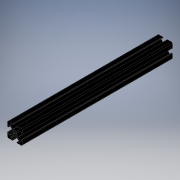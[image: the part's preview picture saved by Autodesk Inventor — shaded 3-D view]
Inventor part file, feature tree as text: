
AUTODESK INVENTOR PART (.ipt)
format: ipt  version: 2019 (Build 230136000, 136)  size: 237,056 bytes
history: native  units: mm
features: extrude x1, sketch x1
ambient origin geometry x8: Origin, YZ Plane, XZ Plane, XY Plane, X Axis, Y Axis, Z Axis, Center Point
bodies: Solid1 (feature_tree)
feature tree (2):
  extrude  "Extrusion1"  [1 undecoded]
  sketch  "Sketch_1"  dims[d0=203.2mm d1=0.0mm]
note: 1 required parameter value undecoded (feature->parameter linkage not recoverable at this tier; creation-order binding heuristic only, values carry confidence <= 0.55)
